# Revit family: Casement_38_C_Side_Hung_Standard
name_source: partatom
category: Windows
revit_build: Autodesk Revit 2014 (Build: 20130308_1515(x64)
units: mm (PartAtom-declared; Revit-internal decimal feet)

## types (12) — shared parameters
Aluminium Thickness = 1 mm  [stored 0.00328084 ft]
Bead SG Gap = 13 mm  [stored 0.0426509 ft]
Casement Dimension = 38 mm  [stored 0.124672 ft]
Custom Sash Left Width = 554 mm  [stored 1.81759 ft]
Custom Sash Right Width = 554 mm  [stored 1.81759 ft]
DG Extrusion Start = 9 mm  [stored 0.0295276 ft]
DG Gasket Finish = Double Glazing Gasket Material
DG Thickness Calc = 4 mm  [stored 0.0131234 ft]
Default Sill Height = 800 mm  [stored 2.62467 ft]
Depth Bead = 24 mm  [stored 0.0787402 ft]
Depth Mullion = 39 mm  [stored 0.127953 ft]
Description = Window 38mm, Type C side hung
Frame Center Offset = 19 mm  [stored 0.062336 ft]
Limit Fixed Pane Width Max = 1500 mm
Limit Fixed Pane Width Min = 200 mm  [stored 0.656168 ft]
Limit Sash Height Max = 1500 mm
Limit Sash Height Min = 300 mm  [stored 0.984252 ft]
Limit Sash Width Max = 700 mm  [stored 2.29659 ft]
Limit Sash Width Min = 300 mm  [stored 0.984252 ft]
Limit Window Height Max = 1546 mm
Limit Window Height Min = 346 mm
Limit Window Width Max = 2700 mm
Limit Window Width Min = 1400 mm
Manufacturer = Crealco
Max System DG One Piece Thickness = 6 mm  [stored 0.019685 ft]
Max System DG Unit Thickness = 25 mm  [stored 0.082021 ft]
Model = Casement 38
Offset Bead Center Reversed = 19 mm  [stored 0.062336 ft]
Offset Fixed Panel Left = 600 mm  [stored 1.9685 ft]
Offset Mullion Left Side = 570 mm  [stored 1.87008 ft]
Offset Mullion Right Side = 570 mm  [stored 1.87008 ft]
Offset Sash Side = 23 mm  [stored 0.0754593 ft]
Offset Sash Top = 23 mm  [stored 0.0754593 ft]
Offset Window Exterior = 19 mm  [stored 0.062336 ft]
SG Gasket Thickness = 6 mm  [stored 0.019685 ft]
Sash Center Offset = 16 mm  [stored 0.0524934 ft]
Sash Overlap = 7 mm  [stored 0.0229659 ft]
Sash Spacing Inner = 8 mm  [stored 0.0262467 ft]
Side Hung Left = Yes
Side Hung Right = No
URL = http://www.crealco.co.za
Wall Closure = By host
Width Bead = 15 mm  [stored 0.0492126 ft]
Width Profile = 30 mm  [stored 0.0984252 ft]
Width Sash Left = 554 mm  [stored 1.81759 ft]
Width Sash Left Opening = 524 mm  [stored 1.71916 ft]
Width Sash Right = 554 mm  [stored 1.81759 ft]
Width Sash Right Opening = 524 mm  [stored 1.71916 ft]
zero-valued in all types: Window Exterior Offset

## per-type parameters (varying)
- 38-1809SS-1000Pa: Area Pane Left=0.35 m²; Area Pane Middle=0.48 m²; Area Pane Right=0.35 m²; Clearvue Insulated LowE SHGC Value=0.492; Clearvue Insulated LowE U Value=3.48; Clearvue Insulated SHGC Value=0.541; Clearvue Insulated U Value=4; Clearvue SHGC Value=0.617; Corrected Mullion Size=0 mm  [stored 0 ft]; Custom Windload=1000 mm  [stored 3.28084 ft]; Custom Window Height=890 mm  [stored 2.91995 ft]; Custom Window Width=1790 mm; Energy Advantage SHGC Value=0.554; Energy Advantage U Value=4.67; Height=890 mm  [stored 2.91995 ft]; Height Fixed Panel Center=830 mm  [stored 2.7231 ft]; Height Sash=814 mm  [stored 2.6706 ft]; Height Sash Opening=844 mm  [stored 2.76903 ft]; Intruderprufe Insulated LowE SHGC Value=0.456; Intruderprufe Insulated LowE U Value=3.4; Intruderprufe Insulated SHGC Value=0.5; Intruderprufe Insulated U Value=3.9; Intruderprufe LowE SHGC Value=0.518; Intruderprufe LowE U Value=4.55; Intruderprufe SHGC Value=0.599; Intruderprufe U Value=6.08; Length Mullion=890 mm  [stored 2.91995 ft]; Max Pane Area=0.48 m²; Mullion Depth Windload Based=39 mm  [stored 0.127953 ft]; Sash Height=845 mm  [stored 2.77231 ft]; Standard Mullion Different=0 mm  [stored 0 ft]; Width=1790 mm; Width Fixed Panel Center=590 mm; Windload Design=1000 mm  [stored 3.28084 ft]
- 38-1809SS-1500Pa: Area Pane Left=0.35 m²; Area Pane Middle=0.48 m²; Area Pane Right=0.35 m²; Clearvue Insulated LowE SHGC Value=0.492; Clearvue Insulated LowE U Value=3.48; Clearvue Insulated SHGC Value=0.541; Clearvue Insulated U Value=4; Clearvue SHGC Value=0.617; Corrected Mullion Size=0 mm  [stored 0 ft]; Custom Windload=1500 mm; Custom Window Height=890 mm  [stored 2.91995 ft]; Custom Window Width=1790 mm; Energy Advantage SHGC Value=0.554; Energy Advantage U Value=4.67; Height=890 mm  [stored 2.91995 ft]; Height Fixed Panel Center=830 mm  [stored 2.7231 ft]; Height Sash=814 mm  [stored 2.6706 ft]; Height Sash Opening=844 mm  [stored 2.76903 ft]; Intruderprufe Insulated LowE SHGC Value=0.456; Intruderprufe Insulated LowE U Value=3.4; Intruderprufe Insulated SHGC Value=0.5; Intruderprufe Insulated U Value=3.9; Intruderprufe LowE SHGC Value=0.518; Intruderprufe LowE U Value=4.55; Intruderprufe SHGC Value=0.599; Intruderprufe U Value=6.08; Length Mullion=890 mm  [stored 2.91995 ft]; Max Pane Area=0.48 m²; Mullion Depth Windload Based=39 mm  [stored 0.127953 ft]; Sash Height=845 mm  [stored 2.77231 ft]; Standard Mullion Different=0 mm  [stored 0 ft]; Width=1790 mm; Width Fixed Panel Center=590 mm; Windload Design=1500 mm
- 38-1809SS-2000Pa: Area Pane Left=0.35 m²; Area Pane Middle=0.48 m²; Area Pane Right=0.35 m²; Clearvue Insulated LowE SHGC Value=0.492; Clearvue Insulated LowE U Value=3.48; Clearvue Insulated SHGC Value=0.541; Clearvue Insulated U Value=4; Clearvue SHGC Value=0.617; Corrected Mullion Size=0 mm  [stored 0 ft]; Custom Windload=2000 mm; Custom Window Height=890 mm  [stored 2.91995 ft]; Custom Window Width=1790 mm; Energy Advantage SHGC Value=0.554; Energy Advantage U Value=4.67; Height=890 mm  [stored 2.91995 ft]; Height Fixed Panel Center=830 mm  [stored 2.7231 ft]; Height Sash=814 mm  [stored 2.6706 ft]; Height Sash Opening=844 mm  [stored 2.76903 ft]; Intruderprufe Insulated LowE SHGC Value=0.456; Intruderprufe Insulated LowE U Value=3.4; Intruderprufe Insulated SHGC Value=0.5; Intruderprufe Insulated U Value=3.9; Intruderprufe LowE SHGC Value=0.518; Intruderprufe LowE U Value=4.55; Intruderprufe SHGC Value=0.599; Intruderprufe U Value=6.08; Length Mullion=890 mm  [stored 2.91995 ft]; Max Pane Area=0.48 m²; Mullion Depth Windload Based=39 mm  [stored 0.127953 ft]; Sash Height=845 mm  [stored 2.77231 ft]; Standard Mullion Different=0 mm  [stored 0 ft]; Width=1790 mm; Width Fixed Panel Center=590 mm; Windload Design=2000 mm
- 38-2409SS-1000Pa: Area Pane Left=0.35 m²; Area Pane Middle=0.97 m²; Area Pane Right=0.35 m²; Clearvue Insulated LowE SHGC Value=0.522; Clearvue Insulated LowE U Value=3.23; Clearvue Insulated SHGC Value=0.573; Clearvue Insulated U Value=3.8; Clearvue SHGC Value=0.654; Corrected Mullion Size=0 mm  [stored 0 ft]; Custom Windload=1000 mm  [stored 3.28084 ft]; Custom Window Height=890 mm  [stored 2.91995 ft]; Custom Window Width=2390 mm; Energy Advantage SHGC Value=0.586; Energy Advantage U Value=4.51; Height=890 mm  [stored 2.91995 ft]; Height Fixed Panel Center=830 mm  [stored 2.7231 ft]; Height Sash=814 mm  [stored 2.6706 ft]; Height Sash Opening=844 mm  [stored 2.76903 ft]; Intruderprufe Insulated LowE SHGC Value=0.482; Intruderprufe Insulated LowE U Value=3.16; Intruderprufe Insulated SHGC Value=0.531; Intruderprufe Insulated U Value=3.71; Intruderprufe LowE SHGC Value=0.548; Intruderprufe LowE U Value=4.4; Intruderprufe SHGC Value=0.629; Intruderprufe U Value=6.02; Length Mullion=890 mm  [stored 2.91995 ft]; Max Pane Area=0.97 m²; Mullion Depth Windload Based=39 mm  [stored 0.127953 ft]; Sash Height=845 mm  [stored 2.77231 ft]; Standard Mullion Different=0 mm  [stored 0 ft]; Width=2390 mm; Width Fixed Panel Center=1190 mm  [stored 3.9042 ft]; Windload Design=1000 mm  [stored 3.28084 ft]
- 38-2409SS-1500Pa: Area Pane Left=0.35 m²; Area Pane Middle=0.97 m²; Area Pane Right=0.35 m²; Clearvue Insulated LowE SHGC Value=0.522; Clearvue Insulated LowE U Value=3.23; Clearvue Insulated SHGC Value=0.573; Clearvue Insulated U Value=3.8; Clearvue SHGC Value=0.654; Corrected Mullion Size=0 mm  [stored 0 ft]; Custom Windload=1500 mm; Custom Window Height=890 mm  [stored 2.91995 ft]; Custom Window Width=2390 mm; Energy Advantage SHGC Value=0.586; Energy Advantage U Value=4.51; Height=890 mm  [stored 2.91995 ft]; Height Fixed Panel Center=830 mm  [stored 2.7231 ft]; Height Sash=814 mm  [stored 2.6706 ft]; Height Sash Opening=844 mm  [stored 2.76903 ft]; Intruderprufe Insulated LowE SHGC Value=0.482; Intruderprufe Insulated LowE U Value=3.16; Intruderprufe Insulated SHGC Value=0.531; Intruderprufe Insulated U Value=3.71; Intruderprufe LowE SHGC Value=0.548; Intruderprufe LowE U Value=4.4; Intruderprufe SHGC Value=0.629; Intruderprufe U Value=6.02; Length Mullion=890 mm  [stored 2.91995 ft]; Max Pane Area=0.97 m²; Mullion Depth Windload Based=39 mm  [stored 0.127953 ft]; Sash Height=845 mm  [stored 2.77231 ft]; Standard Mullion Different=0 mm  [stored 0 ft]; Width=2390 mm; Width Fixed Panel Center=1190 mm  [stored 3.9042 ft]; Windload Design=1500 mm
- 38-2409SS-2000Pa: Area Pane Left=0.35 m²; Area Pane Middle=0.97 m²; Area Pane Right=0.35 m²; Clearvue Insulated LowE SHGC Value=0.522; Clearvue Insulated LowE U Value=3.23; Clearvue Insulated SHGC Value=0.573; Clearvue Insulated U Value=3.8; Clearvue SHGC Value=0.654; Corrected Mullion Size=0 mm  [stored 0 ft]; Custom Windload=2000 mm; Custom Window Height=890 mm  [stored 2.91995 ft]; Custom Window Width=2390 mm; Energy Advantage SHGC Value=0.586; Energy Advantage U Value=4.51; Height=890 mm  [stored 2.91995 ft]; Height Fixed Panel Center=830 mm  [stored 2.7231 ft]; Height Sash=814 mm  [stored 2.6706 ft]; Height Sash Opening=844 mm  [stored 2.76903 ft]; Intruderprufe Insulated LowE SHGC Value=0.482; Intruderprufe Insulated LowE U Value=3.16; Intruderprufe Insulated SHGC Value=0.531; Intruderprufe Insulated U Value=3.71; Intruderprufe LowE SHGC Value=0.548; Intruderprufe LowE U Value=4.4; Intruderprufe SHGC Value=0.629; Intruderprufe U Value=6.02; Length Mullion=890 mm  [stored 2.91995 ft]; Max Pane Area=0.97 m²; Mullion Depth Windload Based=39 mm  [stored 0.127953 ft]; Sash Height=845 mm  [stored 2.77231 ft]; Standard Mullion Different=0 mm  [stored 0 ft]; Width=2390 mm; Width Fixed Panel Center=1190 mm  [stored 3.9042 ft]; Windload Design=2000 mm
- 38-1812SS-1000Pa: Area Pane Left=0.49 m²; Area Pane Middle=0.65 m²; Area Pane Right=0.49 m²; Clearvue Insulated LowE SHGC Value=0.511; Clearvue Insulated LowE U Value=3.34; Clearvue Insulated SHGC Value=0.561; Clearvue Insulated U Value=3.88; Clearvue SHGC Value=0.641; Corrected Mullion Size=0 mm  [stored 0 ft]; Custom Windload=1000 mm  [stored 3.28084 ft]; Custom Window Height=1190 mm  [stored 3.9042 ft]; Custom Window Width=1790 mm; Energy Advantage SHGC Value=0.575; Energy Advantage U Value=4.58; Height=1190 mm  [stored 3.9042 ft]; Height Fixed Panel Center=1130 mm  [stored 3.70735 ft]; Height Sash=1114 mm  [stored 3.65486 ft]; Height Sash Opening=1144 mm; Intruderprufe Insulated LowE SHGC Value=0.472; Intruderprufe Insulated LowE U Value=3.26; Intruderprufe Insulated SHGC Value=0.519; Intruderprufe Insulated U Value=3.79; Intruderprufe LowE SHGC Value=0.537; Intruderprufe LowE U Value=4.47; Intruderprufe SHGC Value=0.621; Intruderprufe U Value=6.06; Length Mullion=1190 mm  [stored 3.9042 ft]; Max Pane Area=0.65 m²; Mullion Depth Windload Based=39 mm  [stored 0.127953 ft]; Sash Height=1145 mm  [stored 3.75656 ft]; Standard Mullion Different=0 mm  [stored 0 ft]; Width=1790 mm; Width Fixed Panel Center=590 mm; Windload Design=1000 mm  [stored 3.28084 ft]
- 38-1812SS-1500Pa: Area Pane Left=0.49 m²; Area Pane Middle=0.65 m²; Area Pane Right=0.49 m²; Clearvue Insulated LowE SHGC Value=0.511; Clearvue Insulated LowE U Value=3.34; Clearvue Insulated SHGC Value=0.561; Clearvue Insulated U Value=3.88; Clearvue SHGC Value=0.641; Corrected Mullion Size=0 mm  [stored 0 ft]; Custom Windload=1500 mm; Custom Window Height=1190 mm  [stored 3.9042 ft]; Custom Window Width=1790 mm; Energy Advantage SHGC Value=0.575; Energy Advantage U Value=4.58; Height=1190 mm  [stored 3.9042 ft]; Height Fixed Panel Center=1130 mm  [stored 3.70735 ft]; Height Sash=1114 mm  [stored 3.65486 ft]; Height Sash Opening=1144 mm; Intruderprufe Insulated LowE SHGC Value=0.472; Intruderprufe Insulated LowE U Value=3.26; Intruderprufe Insulated SHGC Value=0.519; Intruderprufe Insulated U Value=3.79; Intruderprufe LowE SHGC Value=0.537; Intruderprufe LowE U Value=4.47; Intruderprufe SHGC Value=0.621; Intruderprufe U Value=6.06; Length Mullion=1190 mm  [stored 3.9042 ft]; Max Pane Area=0.65 m²; Mullion Depth Windload Based=39 mm  [stored 0.127953 ft]; Sash Height=1145 mm  [stored 3.75656 ft]; Standard Mullion Different=0 mm  [stored 0 ft]; Width=1790 mm; Width Fixed Panel Center=590 mm; Windload Design=1500 mm
- 38-1812SS-2000Pa: Area Pane Left=0.49 m²; Area Pane Middle=0.65 m²; Area Pane Right=0.49 m²; Clearvue Insulated LowE SHGC Value=0.511; Clearvue Insulated LowE U Value=3.34; Clearvue Insulated SHGC Value=0.561; Clearvue Insulated U Value=3.88; Clearvue SHGC Value=0.641; Corrected Mullion Size=39 mm  [stored 0.127953 ft]; Custom Windload=2000 mm; Custom Window Height=1190 mm  [stored 3.9042 ft]; Custom Window Width=1790 mm; Energy Advantage SHGC Value=0.575; Energy Advantage U Value=4.58; Height=1190 mm  [stored 3.9042 ft]; Height Fixed Panel Center=1130 mm  [stored 3.70735 ft]; Height Sash=1114 mm  [stored 3.65486 ft]; Height Sash Opening=1144 mm; Intruderprufe Insulated LowE SHGC Value=0.472; Intruderprufe Insulated LowE U Value=3.26; Intruderprufe Insulated SHGC Value=0.519; Intruderprufe Insulated U Value=3.79; Intruderprufe LowE SHGC Value=0.537; Intruderprufe LowE U Value=4.47; Intruderprufe SHGC Value=0.621; Intruderprufe U Value=6.06; Length Mullion=1190 mm  [stored 3.9042 ft]; Max Pane Area=0.65 m²; Mullion Depth Windload Based=39 mm  [stored 0.127953 ft]; Sash Height=1145 mm  [stored 3.75656 ft]; Standard Mullion Different=1 mm  [stored 0.00328084 ft]; Width=1790 mm; Width Fixed Panel Center=590 mm; Windload Design=2000 mm
- 38-2412SS-1000Pa: Area Pane Left=0.49 m²; Area Pane Middle=1.32 m²; Area Pane Right=0.49 m²; Clearvue Insulated LowE SHGC Value=0.54; Clearvue Insulated LowE U Value=3.09; Clearvue Insulated SHGC Value=0.594; Clearvue Insulated U Value=3.68; Clearvue SHGC Value=0.677; Corrected Mullion Size=0 mm  [stored 0 ft]; Custom Windload=1000 mm  [stored 3.28084 ft]; Custom Window Height=1190 mm  [stored 3.9042 ft]; Custom Window Width=2390 mm; Energy Advantage SHGC Value=0.606; Energy Advantage U Value=4.42; Height=1190 mm  [stored 3.9042 ft]; Height Fixed Panel Center=1130 mm  [stored 3.70735 ft]; Height Sash=1114 mm  [stored 3.65486 ft]; Height Sash Opening=1144 mm; Intruderprufe Insulated LowE SHGC Value=0.498; Intruderprufe Insulated LowE U Value=3.02; Intruderprufe Insulated SHGC Value=0.549; Intruderprufe Insulated U Value=3.59; Intruderprufe LowE SHGC Value=0.566; Intruderprufe LowE U Value=4.32; Intruderprufe SHGC Value=0.651; Intruderprufe U Value=6; Length Mullion=1190 mm  [stored 3.9042 ft]; Max Pane Area=1.32 m²; Mullion Depth Windload Based=39 mm  [stored 0.127953 ft]; Sash Height=1145 mm  [stored 3.75656 ft]; Standard Mullion Different=0 mm  [stored 0 ft]; Width=2390 mm; Width Fixed Panel Center=1190 mm  [stored 3.9042 ft]; Windload Design=1000 mm  [stored 3.28084 ft]
- 38-2412SS-1500Pa: Area Pane Left=0.49 m²; Area Pane Middle=1.32 m²; Area Pane Right=0.49 m²; Clearvue Insulated LowE SHGC Value=0.54; Clearvue Insulated LowE U Value=3.09; Clearvue Insulated SHGC Value=0.594; Clearvue Insulated U Value=3.68; Clearvue SHGC Value=0.677; Corrected Mullion Size=0 mm  [stored 0 ft]; Custom Windload=1500 mm; Custom Window Height=1190 mm  [stored 3.9042 ft]; Custom Window Width=2390 mm; Energy Advantage SHGC Value=0.606; Energy Advantage U Value=4.42; Height=1190 mm  [stored 3.9042 ft]; Height Fixed Panel Center=1130 mm  [stored 3.70735 ft]; Height Sash=1114 mm  [stored 3.65486 ft]; Height Sash Opening=1144 mm; Intruderprufe Insulated LowE SHGC Value=0.498; Intruderprufe Insulated LowE U Value=3.02; Intruderprufe Insulated SHGC Value=0.549; Intruderprufe Insulated U Value=3.59; Intruderprufe LowE SHGC Value=0.566; Intruderprufe LowE U Value=4.32; Intruderprufe SHGC Value=0.651; Intruderprufe U Value=6; Length Mullion=1190 mm  [stored 3.9042 ft]; Max Pane Area=1.32 m²; Mullion Depth Windload Based=39 mm  [stored 0.127953 ft]; Sash Height=1145 mm  [stored 3.75656 ft]; Standard Mullion Different=0 mm  [stored 0 ft]; Width=2390 mm; Width Fixed Panel Center=1190 mm  [stored 3.9042 ft]; Windload Design=1500 mm
- 38-2412SS-2000Pa: Area Pane Left=0.49 m²; Area Pane Middle=1.32 m²; Area Pane Right=0.49 m²; Clearvue Insulated LowE SHGC Value=0.541; Clearvue Insulated LowE U Value=3.15; Clearvue Insulated SHGC Value=0.594; Clearvue Insulated U Value=3.74; Clearvue SHGC Value=0.676; Corrected Mullion Size=0 mm  [stored 0 ft]; Custom Windload=2000 mm; Custom Window Height=1190 mm  [stored 3.9042 ft]; Custom Window Width=2390 mm; Energy Advantage SHGC Value=0.605; Energy Advantage U Value=4.49; Height=1190 mm  [stored 3.9042 ft]; Height Fixed Panel Center=1130 mm  [stored 3.70735 ft]; Height Sash=1114 mm  [stored 3.65486 ft]; Height Sash Opening=1144 mm; Intruderprufe Insulated LowE SHGC Value=0.5; Intruderprufe Insulated LowE U Value=3.08; Intruderprufe Insulated SHGC Value=0.552; Intruderprufe Insulated U Value=3.65; Intruderprufe LowE SHGC Value=0.568; Intruderprufe LowE U Value=4.39; Intruderprufe SHGC Value=0.638; Intruderprufe U Value=6.02; Length Mullion=1190 mm  [stored 3.9042 ft]; Max Pane Area=1.32 m²; Mullion Depth Windload Based=54 mm  [stored 0.177165 ft]; Sash Height=1145 mm  [stored 3.75656 ft]; Standard Mullion Different=0 mm  [stored 0 ft]; Width=2390 mm; Width Fixed Panel Center=1190 mm  [stored 3.9042 ft]; Windload Design=2000 mm

note: [stored X ft] marks values corroborated as IEEE doubles in the binary element streams (Revit-internal decimal feet)

## geometry (parser evidence)
native form markers: Extrusion x1, Sweep x29
no freeform markers — native parametric forms only
